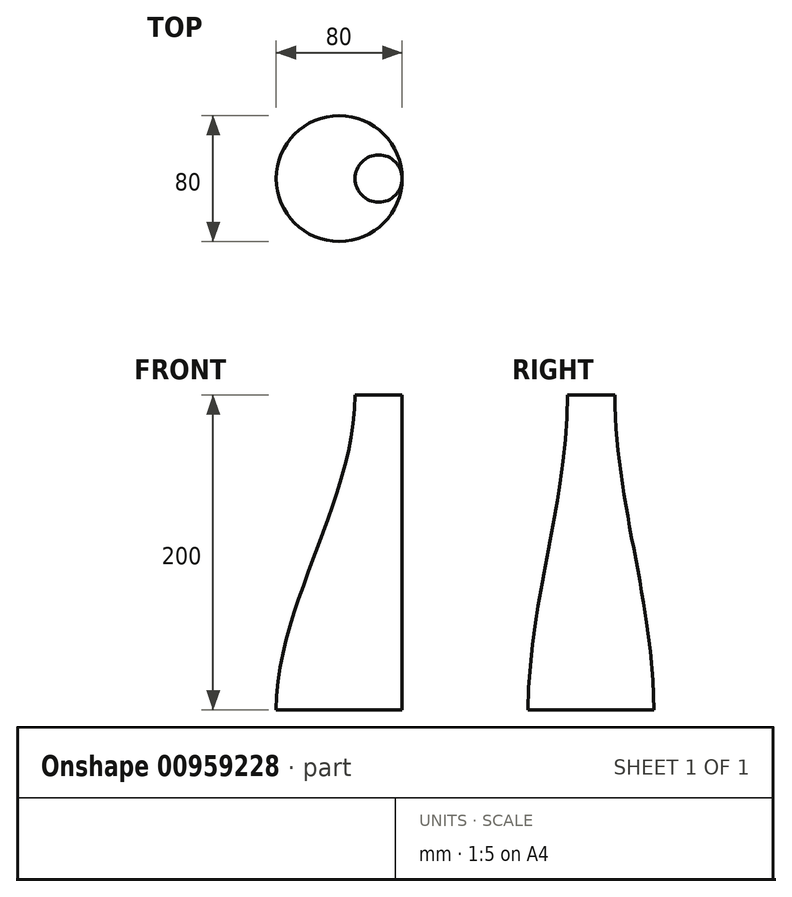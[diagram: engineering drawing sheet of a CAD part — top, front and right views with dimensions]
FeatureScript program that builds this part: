
annotation { "Feature Type Name" : "Feature", "Feature Type Description" : "" }
export const myFeature = defineFeature(function(context is Context, id is Id, definition is map)
    precondition{}
    {
        {
            var Q0;
            Q0=qCreatedBy(makeId("Top.planeOp"),FACE);
            var sketch = newSketch(context, id + "F0", { "sketchPlane" : qUnion([Q0])});
            skCircle(sketch, "E0", {"center": v(0, 0) * mm, "radius": 40 * mm});
            skSolve(sketch);
        }
        {
            var Q0;
            Q0=qCreatedBy(makeId("Top.planeOp"),FACE);
            cPlane(context, id + "F1", {"entities" : qUnion([Q0]), "cplaneType" : CPlaneType.OFFSET, "offset" : 200 * mm, "width" : 150 * mm, "height" : 150 * mm});
        }
        {
            var Q0;
            Q0=qCreatedBy(id+"F1.planeOp",FACE);
            var sketch = newSketch(context, id + "F2", { "sketchPlane" : qUnion([Q0])});
            skCircle(sketch, "E1", {"center": v(25, 0) * mm, "radius": 15 * mm});
            skSolve(sketch);
        }
        {
            var Q0;
            Q0=makeQuery(id+"F0.imprint","IMPRINT",FACE,{"disambiguationData":[TD([[makeQuery(id+"F0.imprint","IMPRINT",EDGE,{"derivedFrom":sQuery(id+"F0.wireOp",EDGE,"E0")}),1.0]])]});
            var Q1;
            Q1=makeQuery(id+"F2.imprint","IMPRINT",FACE,{"disambiguationData":[TD([[makeQuery(id+"F2.imprint","IMPRINT",EDGE,{"derivedFrom":sQuery(id+"F2.wireOp",EDGE,"E1")}),1.0]])]});
            loft(context, id + "F3", {"startCondition" : LoftEndDerivativeType.NORMAL_TO_PROFILE, "startMagnitude" : 1, "endCondition" : LoftEndDerivativeType.NORMAL_TO_PROFILE, "endMagnitude" : 1, "sheetProfilesArray" : [{ "sheetProfileEntities" : qUnion([Q0]) }, { "sheetProfileEntities" : qUnion([Q1]) }]});
        }
    });
